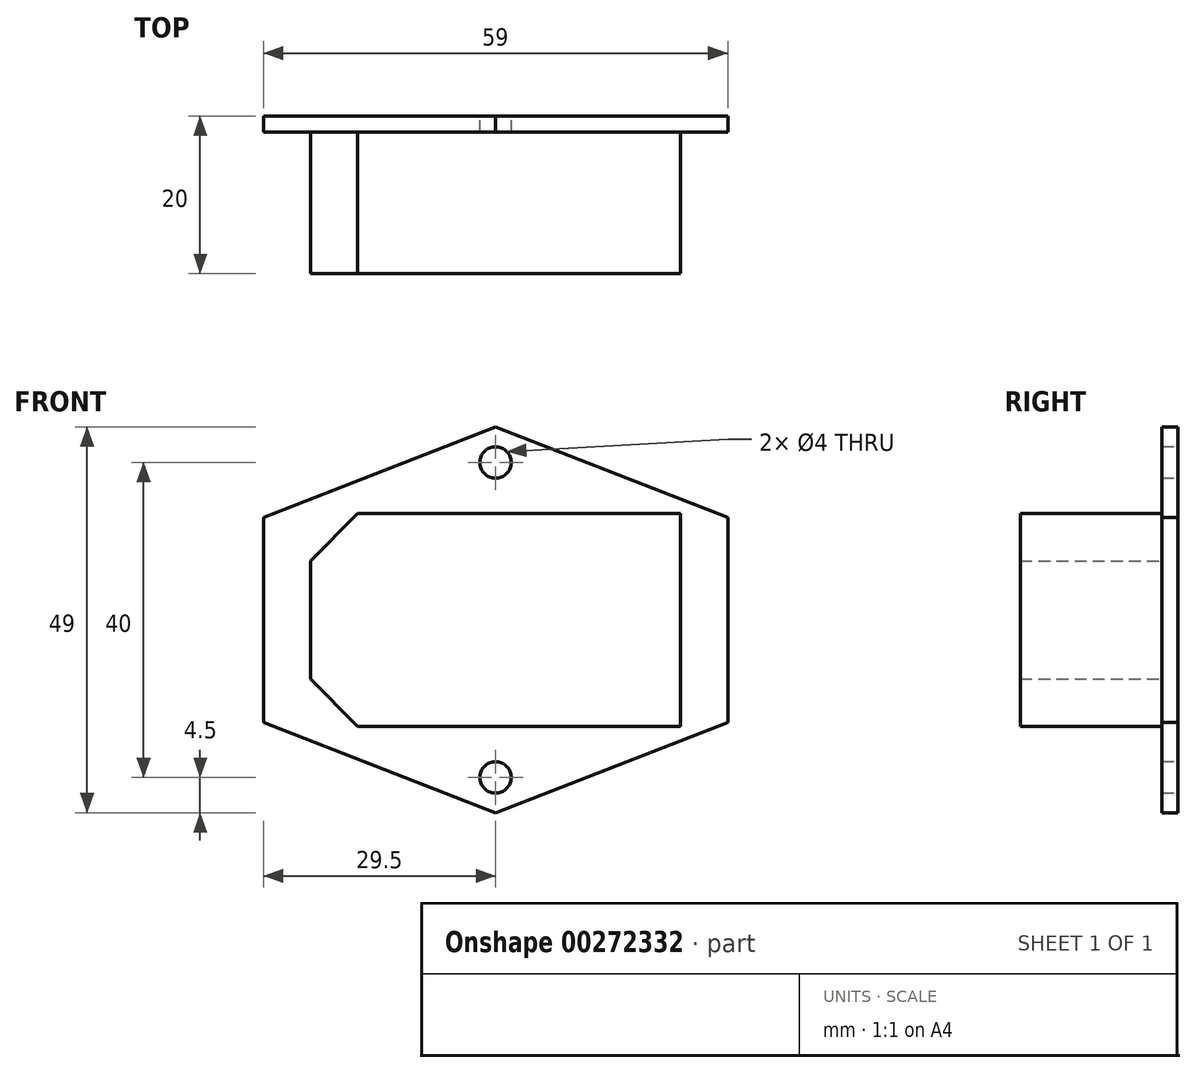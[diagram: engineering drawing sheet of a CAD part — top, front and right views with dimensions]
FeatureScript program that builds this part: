
annotation { "Feature Type Name" : "Feature", "Feature Type Description" : "" }
export const myFeature = defineFeature(function(context is Context, id is Id, definition is map)
    precondition{}
    {
        {
            var Q0;
            Q0=qCreatedBy(makeId("Front.planeOp"),FACE);
            var sketch = newSketch(context, id + "F0", { "sketchPlane" : qUnion([Q0])});
            skLineSegment(sketch, "E0", {"start": v(0, 24.5) * mm, "end": v(0, -24.5) * mm, "construction": true});
            skLineSegment(sketch, "E1", {"start": v(-29.5, 13) * mm, "end": v(-29.5, -13) * mm});
            skLineSegment(sketch, "E2", {"start": v(29.5, 13) * mm, "end": v(29.5, -13) * mm});
            skLineSegment(sketch, "E3", {"start": v(-29.5, 13) * mm, "end": v(0, 24.5) * mm});
            skLineSegment(sketch, "E4", {"start": v(0, 24.5) * mm, "end": v(29.5, 13) * mm});
            skLineSegment(sketch, "E5", {"start": v(29.5, -13) * mm, "end": v(0, -24.5) * mm});
            skLineSegment(sketch, "E6", {"start": v(0, -24.5) * mm, "end": v(-29.5, -13) * mm});
            skLineSegment(sketch, "E7", {"start": v(-29.5, 0) * mm, "end": v(29.5, 0) * mm, "construction": true});
            skCircle(sketch, "E8", {"center": v(0, 20) * mm, "radius": 2 * mm});
            skCircle(sketch, "E9", {"center": v(0, -20) * mm, "radius": 2 * mm});
            skLineSegment(sketch, "E10", {"start": v(0, 20) * mm, "end": v(0, -20) * mm});
            skPoint(sketch, "E11", {"position": v(0, 0) * mm});
            skLineSegment(sketch, "E12.bottom", {"start": v(-17.5, 13.5) * mm, "end": v(23.5, 13.5) * mm});
            skLineSegment(sketch, "E12.top", {"start": v(-17.5, -13.5) * mm, "end": v(23.5, -13.5) * mm});
            skLineSegment(sketch, "E12.right", {"start": v(23.5, 13.5) * mm, "end": v(23.5, -13.5) * mm});
            skLineSegment(sketch, "E13", {"start": v(-23.5, 7.5) * mm, "end": v(-23.5, -7.5) * mm});
            skLineSegment(sketch, "E14", {"start": v(-23.5, -7.5) * mm, "end": v(-17.5, -13.5) * mm});
            skLineSegment(sketch, "E15", {"start": v(-23.5, 7.5) * mm, "end": v(-17.5, 13.5) * mm});
            skLineSegment(sketch, "E16", {"start": v(23.5, 0) * mm, "end": v(-23.5, 0) * mm, "construction": true});
            skPoint(sketch, "E16.endSnap0", {"position": v(23.5, 0) * mm});
            skLineSegment(sketch, "E17", {"start": v(-17.5, 13.5) * mm, "end": v(-17.5, -13.5) * mm, "construction": true});
            skSolve(sketch);
        }
        {
            var Q0;
            Q0=makeQuery(id+"F0.imprint","IMPRINT",FACE,{"disambiguationData":[TD([[makeQuery(id+"F0.imprint","IMPRINT",EDGE,{"derivedFrom":sQuery(id+"F0.wireOp",EDGE,"E1")}),1.0]])]});
            extrude(context, id + "F1", {"entities" : qUnion([Q0]), "depth" : 2 * mm});
        }
        {
            var Q0;
            Q0=makeQuery(id+"F0.imprint","IMPRINT",FACE,{"disambiguationData":[TD([[makeQuery(id+"F0.imprint","IMPRINT",EDGE,{"derivedFrom":sQuery(id+"F0.wireOp",EDGE,"E13")}),1.0]])]});
            var Q1;
            {var subQ5=sQuery(id+"F0.wireOp",EDGE,"E12.right");Q1=makeQuery(id+"F0.imprint","IMPRINT",FACE,{"disambiguationData":[TD([[makeQuery(id+"F0.imprint","IMPRINT",EDGE,{"derivedFrom":subQ5}),-1.0]])]});}
            extrude(context, id + "F2", {"entities" : qUnion([Q0, Q1]), "operationType" : NewBodyOperationType.ADD, "depth" : 20 * mm});
        }
    });
